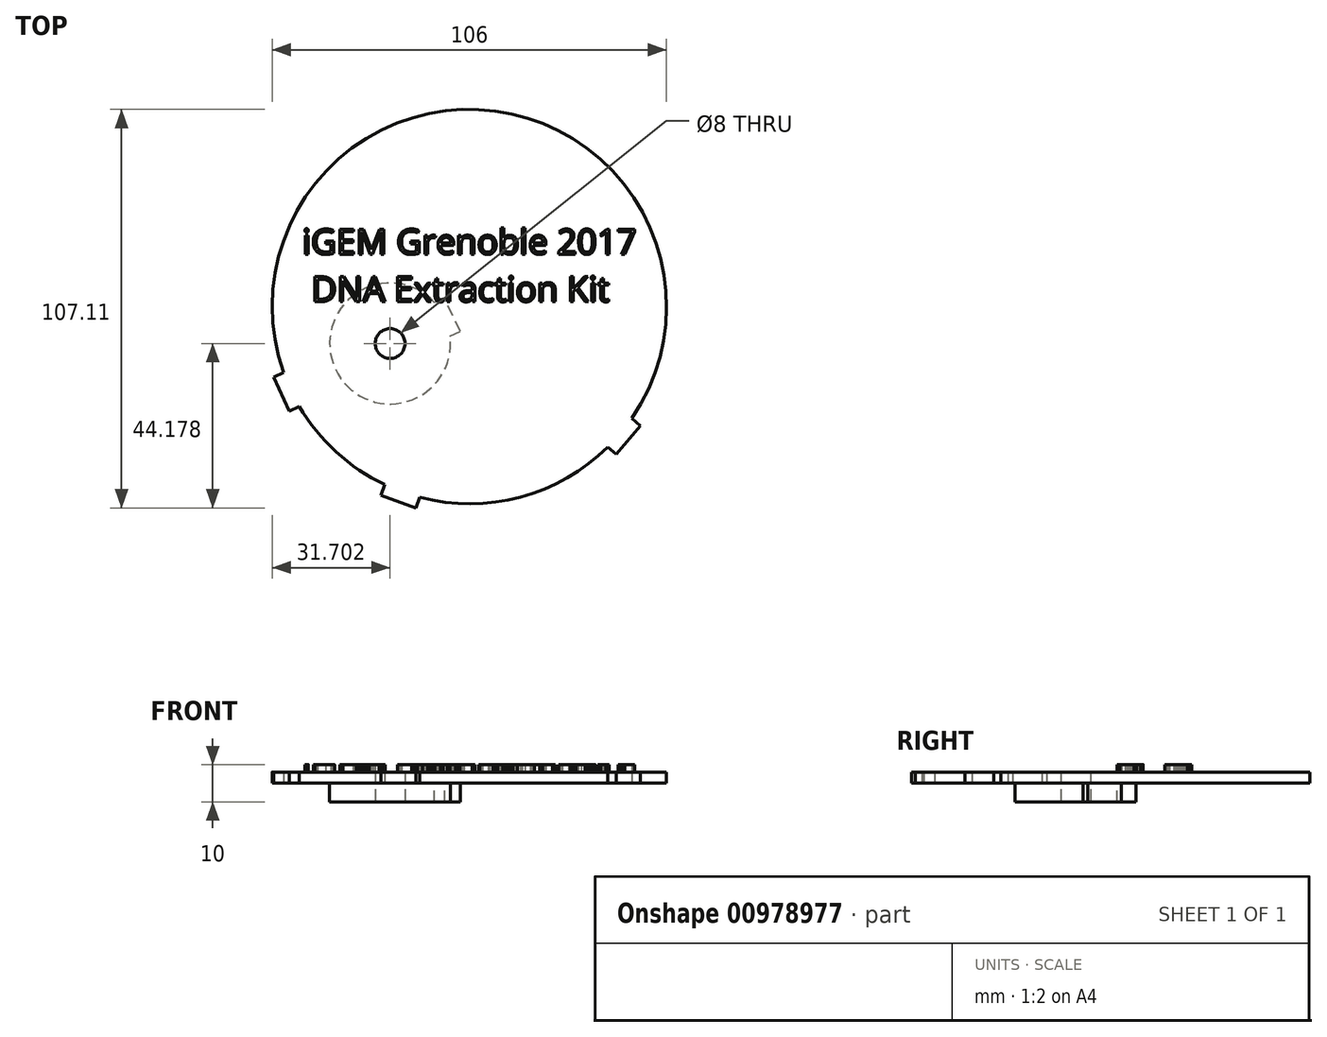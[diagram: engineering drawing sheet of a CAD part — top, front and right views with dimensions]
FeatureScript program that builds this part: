
annotation { "Feature Type Name" : "Feature", "Feature Type Description" : "" }
export const myFeature = defineFeature(function(context is Context, id is Id, definition is map)
    precondition{}
    {
        {
            var Q0;
            Q0=qCreatedBy(makeId("Top.planeOp"),FACE);
            var sketch = newSketch(context, id + "F0", { "sketchPlane" : qUnion([Q0])});
            skCircle(sketch, "E0", {"center": v(0, 0) * mm, "radius": 53 * mm});
            skSolve(sketch);
        }
        {
            var Q0;
            Q0=makeQuery(id+"F0.imprint","IMPRINT",FACE,{"disambiguationData":[TD([[makeQuery(id+"F0.imprint","IMPRINT",EDGE,{"derivedFrom":sQuery(id+"F0.wireOp",EDGE,"E0")}),1.0]])]});
            extrude(context, id + "F1", {"entities" : qUnion([Q0]), "depth" : 3 * mm, "offsetDistance" : 25 * mm});
        }
        {
            var Q0;
            Q0=makeQuery(id+"F1.opExtrude","CAP_FACE",FACE,{"disambiguationData":[OSD([sQuery(id+"F0.wireOp",EDGE,"E0")])],"isStart":true});
            var sketch = newSketch(context, id + "F2", { "sketchPlane" : qUnion([Q0])});
            skCircle(sketch, "E1", {"center": v(-21.3, 9.93) * mm, "radius": 16.25 * mm});
            skLineSegment(sketch, "E2", {"start": v(0, 0) * mm, "end": v(-21.3, 9.93) * mm});
            skLineSegment(sketch, "E3", {"start": v(0, 0) * mm, "end": v(0, 31.72) * mm});
            skLineSegment(sketch, "E4", {"start": v(-5.17, 7.93) * mm, "end": v(-2.45, 6.66) * mm});
            skLineSegment(sketch, "E5", {"start": v(-2.45, 6.66) * mm, "end": v(-6.68, -2.4) * mm});
            skLineSegment(sketch, "E6", {"start": v(-6.68, -2.4) * mm, "end": v(-9.4, -1.13) * mm});
            skLineSegment(sketch, "E7", {"start": v(0, 0) * mm, "end": v(-18.13, 49.8) * mm});
            skLineSegment(sketch, "E8", {"start": v(0, 0) * mm, "end": v(40.6, 34.07) * mm});
            skLineSegment(sketch, "E9", {"start": v(-49.93, 17.77) * mm, "end": v(-52.65, 19.04) * mm});
            skLineSegment(sketch, "E10", {"start": v(-52.65, 19.04) * mm, "end": v(-48.43, 28.1) * mm});
            skLineSegment(sketch, "E11", {"start": v(-48.43, 28.1) * mm, "end": v(-45.7, 26.83) * mm});
            skLineSegment(sketch, "E12", {"start": v(-22.74, 47.87) * mm, "end": v(-23.77, 50.7) * mm});
            skLineSegment(sketch, "E13", {"start": v(-23.77, 50.7) * mm, "end": v(-14.37, 54.11) * mm});
            skLineSegment(sketch, "E14", {"start": v(-14.37, 54.11) * mm, "end": v(-13.35, 51.3) * mm});
            skLineSegment(sketch, "E15", {"start": v(37.2, 37.75) * mm, "end": v(39.5, 39.67) * mm});
            skLineSegment(sketch, "E16", {"start": v(39.5, 39.67) * mm, "end": v(45.93, 32.01) * mm});
            skLineSegment(sketch, "E17", {"start": v(45.93, 32.01) * mm, "end": v(43.63, 30.09) * mm});
            skSolve(sketch);
        }
        {
            var Q0;
            Q0=makeQuery(id+"F2.imprint","IMPRINT",FACE,{"disambiguationData":[TD([[makeQuery(id+"F2.imprint","IMPRINT",EDGE,{"derivedFrom":sQuery(id+"F2.wireOp",EDGE,"E1")}),1.0]])]});
            var Q1;
            {var subQ0=sQuery(id+"F2.wireOp",EDGE,"E6");Q1=makeQuery(id+"F2.imprint","IMPRINT",FACE,{"disambiguationData":[TD([[makeQuery(id+"F2.imprint","IMPRINT",EDGE,{"derivedFrom":subQ0}),-1.0]])]});}
            var Q2;
            {var subQ0=sQuery(id+"F2.wireOp",EDGE,"E4");Q2=makeQuery(id+"F2.imprint","IMPRINT",FACE,{"disambiguationData":[TD([[makeQuery(id+"F2.imprint","IMPRINT",EDGE,{"derivedFrom":subQ0}),-1.0]])]});}
            extrude(context, id + "F3", {"entities" : qUnion([Q0, Q1, Q2]), "operationType" : NewBodyOperationType.ADD, "depth" : 5 * mm, "offsetDistance" : 25 * mm});
        }
        {
            var Q0;
            Q0=makeQuery(id+"F3.opExtrude","CAP_FACE",FACE,{"disambiguationData":[OSD([sQuery(id+"F2.wireOp",EDGE,"E1")])],"isStart":false});
            var sketch = newSketch(context, id + "F4", { "sketchPlane" : qUnion([Q0])});
            skCircle(sketch, "E18", {"center": v(-21.3, 9.93) * mm, "radius": 4 * mm});
            skSolve(sketch);
        }
        {
            var Q0;
            Q0=makeQuery(id+"F4.imprint","IMPRINT",FACE,{"disambiguationData":[TD([[makeQuery(id+"F4.imprint","IMPRINT",EDGE,{"derivedFrom":sQuery(id+"F4.wireOp",EDGE,"E18")}),1.0]])]});
            extrude(context, id + "F5", {"entities" : qUnion([Q0]), "operationType" : NewBodyOperationType.REMOVE, "oppositeDirection" : true, "depth" : 25 * mm, "offsetDistance" : 25 * mm});
        }
        {
            var Q0;
            {var subQ0=sQuery(id+"F2.wireOp",EDGE,"E9");Q0=makeQuery(id+"F2.imprint","IMPRINT",FACE,{"disambiguationData":[TD([[makeQuery(id+"F2.imprint","IMPRINT",EDGE,{"derivedFrom":subQ0}),-1.0]])]});}
            var Q1;
            {var subQ2=sQuery(id+"F2.wireOp",EDGE,"E12");Q1=makeQuery(id+"F2.imprint","IMPRINT",FACE,{"disambiguationData":[TD([[makeQuery(id+"F2.imprint","IMPRINT",EDGE,{"derivedFrom":subQ2}),-1.0]])]});}
            var Q2;
            {var subQ2=sQuery(id+"F2.wireOp",EDGE,"E15");Q2=makeQuery(id+"F2.imprint","IMPRINT",FACE,{"disambiguationData":[TD([[makeQuery(id+"F2.imprint","IMPRINT",EDGE,{"derivedFrom":subQ2}),-1.0]])]});}
            extrude(context, id + "F6", {"entities" : qUnion([Q0, Q1, Q2]), "operationType" : NewBodyOperationType.ADD, "oppositeDirection" : true, "depth" : 3 * mm, "offsetDistance" : 25 * mm});
        }
        {
            var Q0;
            {var subQ0=sQuery(id+"F0.wireOp",EDGE,"E0");Q0=makeQuery(id+"F6.boolean.opBoolean","MERGE",FACE,{"derivedFrom":[makeQuery(id+"F1.opExtrude","CAP_FACE",FACE,{"disambiguationData":[OSD([subQ0])],"isStart":false}),makeQuery(id+"F6.opExtrude","CAP_FACE",FACE,{"disambiguationData":[OSD([subQ0,sQuery(id+"F2.wireOp",EDGE,"E9"),sQuery(id+"F2.wireOp",EDGE,"E10"),sQuery(id+"F2.wireOp",EDGE,"E11")])],"isStart":false}),makeQuery(id+"F6.opExtrude","CAP_FACE",FACE,{"disambiguationData":[OSD([subQ0,sQuery(id+"F2.wireOp",EDGE,"E12"),sQuery(id+"F2.wireOp",EDGE,"E13"),sQuery(id+"F2.wireOp",EDGE,"E14")])],"isStart":false}),makeQuery(id+"F6.opExtrude","CAP_FACE",FACE,{"disambiguationData":[OSD([subQ0,sQuery(id+"F2.wireOp",EDGE,"E15"),sQuery(id+"F2.wireOp",EDGE,"E16"),sQuery(id+"F2.wireOp",EDGE,"E17")])],"isStart":false})]});}
            var sketch = newSketch(context, id + "F7", { "sketchPlane" : qUnion([Q0])});
            skText(sketch, "E19", { "text": "iGEM Grenoble 2017\n DNA Extraction Kit", "fontName": "OpenSans-Regular.ttf"});
            const initialGuessF7  = {"E19": [-0.04492, 0.01408, 1, 0, 0.00675]};
            skSetInitialGuess(sketch, initialGuessF7);
            skSolve(sketch);
        }
        {
            var Q0;
            Q0=makeQuery(id+"F7.imprint","IMPRINT",FACE,{"disambiguationData":[TD([[makeQuery(id+"F7.imprint","IMPRINT",EDGE,{"derivedFrom":sQuery(id+"F7.wireOp",EDGE,"E19.sketch_text.stroke-0")}),-1.0]])]});
            var Q1;
            Q1=makeQuery(id+"F7.imprint","IMPRINT",FACE,{"disambiguationData":[TD([[makeQuery(id+"F7.imprint","IMPRINT",EDGE,{"derivedFrom":sQuery(id+"F7.wireOp",EDGE,"E19.sketch_text.stroke-4")}),-1.0]])]});
            var Q2;
            Q2=makeQuery(id+"F7.imprint","IMPRINT",FACE,{"disambiguationData":[TD([[makeQuery(id+"F7.imprint","IMPRINT",EDGE,{"derivedFrom":sQuery(id+"F7.wireOp",EDGE,"E19.sketch_text.stroke-12")}),-1.0]])]});
            var Q3;
            Q3=makeQuery(id+"F7.imprint","IMPRINT",FACE,{"disambiguationData":[TD([[makeQuery(id+"F7.imprint","IMPRINT",EDGE,{"derivedFrom":sQuery(id+"F7.wireOp",EDGE,"E19.sketch_text.stroke-32")}),-1.0]])]});
            var Q4;
            Q4=makeQuery(id+"F7.imprint","IMPRINT",FACE,{"disambiguationData":[TD([[makeQuery(id+"F7.imprint","IMPRINT",EDGE,{"derivedFrom":sQuery(id+"F7.wireOp",EDGE,"E19.sketch_text.stroke-44")}),-1.0]])]});
            var Q5;
            Q5=makeQuery(id+"F7.imprint","IMPRINT",FACE,{"disambiguationData":[TD([[makeQuery(id+"F7.imprint","IMPRINT",EDGE,{"derivedFrom":sQuery(id+"F7.wireOp",EDGE,"E19.sketch_text.stroke-62")}),-1.0]])]});
            var Q6;
            Q6=makeQuery(id+"F7.imprint","IMPRINT",FACE,{"disambiguationData":[TD([[makeQuery(id+"F7.imprint","IMPRINT",EDGE,{"derivedFrom":sQuery(id+"F7.wireOp",EDGE,"E19.sketch_text.stroke-82")}),-1.0]])]});
            var Q7;
            Q7=makeQuery(id+"F7.imprint","IMPRINT",FACE,{"disambiguationData":[TD([[makeQuery(id+"F7.imprint","IMPRINT",EDGE,{"derivedFrom":sQuery(id+"F7.wireOp",EDGE,"E19.sketch_text.stroke-95")}),-1.0]])]});
            var Q8;
            Q8=makeQuery(id+"F7.imprint","IMPRINT",FACE,{"disambiguationData":[TD([[makeQuery(id+"F7.imprint","IMPRINT",EDGE,{"derivedFrom":sQuery(id+"F7.wireOp",EDGE,"E19.sketch_text.stroke-114")}),-1.0]])]});
            var Q9;
            Q9=makeQuery(id+"F7.imprint","IMPRINT",FACE,{"disambiguationData":[TD([[makeQuery(id+"F7.imprint","IMPRINT",EDGE,{"derivedFrom":sQuery(id+"F7.wireOp",EDGE,"E19.sketch_text.stroke-131")}),-1.0]])]});
            var Q10;
            Q10=makeQuery(id+"F7.imprint","IMPRINT",FACE,{"disambiguationData":[TD([[makeQuery(id+"F7.imprint","IMPRINT",EDGE,{"derivedFrom":sQuery(id+"F7.wireOp",EDGE,"E19.sketch_text.stroke-148")}),-1.0]])]});
            var Q11;
            Q11=makeQuery(id+"F7.imprint","IMPRINT",FACE,{"disambiguationData":[TD([[makeQuery(id+"F7.imprint","IMPRINT",EDGE,{"derivedFrom":sQuery(id+"F7.wireOp",EDGE,"E19.sketch_text.stroke-171")}),-1.0]])]});
            var Q12;
            Q12=makeQuery(id+"F7.imprint","IMPRINT",FACE,{"disambiguationData":[TD([[makeQuery(id+"F7.imprint","IMPRINT",EDGE,{"derivedFrom":sQuery(id+"F7.wireOp",EDGE,"E19.sketch_text.stroke-175")}),-1.0]])]});
            var Q13;
            Q13=makeQuery(id+"F7.imprint","IMPRINT",FACE,{"disambiguationData":[TD([[makeQuery(id+"F7.imprint","IMPRINT",EDGE,{"derivedFrom":sQuery(id+"F7.wireOp",EDGE,"E19.sketch_text.stroke-194")}),-1.0]])]});
            var Q14;
            Q14=makeQuery(id+"F7.imprint","IMPRINT",FACE,{"disambiguationData":[TD([[makeQuery(id+"F7.imprint","IMPRINT",EDGE,{"derivedFrom":sQuery(id+"F7.wireOp",EDGE,"E19.sketch_text.stroke-214")}),-1.0]])]});
            var Q15;
            Q15=makeQuery(id+"F7.imprint","IMPRINT",FACE,{"disambiguationData":[TD([[makeQuery(id+"F7.imprint","IMPRINT",EDGE,{"derivedFrom":sQuery(id+"F7.wireOp",EDGE,"E19.sketch_text.stroke-230")}),-1.0]])]});
            var Q16;
            Q16=makeQuery(id+"F7.imprint","IMPRINT",FACE,{"disambiguationData":[TD([[makeQuery(id+"F7.imprint","IMPRINT",EDGE,{"derivedFrom":sQuery(id+"F7.wireOp",EDGE,"E19.sketch_text.stroke-239")}),-1.0]])]});
            var Q17;
            Q17=makeQuery(id+"F7.imprint","IMPRINT",FACE,{"disambiguationData":[TD([[makeQuery(id+"F7.imprint","IMPRINT",EDGE,{"derivedFrom":sQuery(id+"F7.wireOp",EDGE,"E19.sketch_text.stroke-246")}),-1.0]])]});
            var Q18;
            Q18=makeQuery(id+"F7.imprint","IMPRINT",FACE,{"disambiguationData":[TD([[makeQuery(id+"F7.imprint","IMPRINT",EDGE,{"derivedFrom":sQuery(id+"F7.wireOp",EDGE,"E19.sketch_text.stroke-260")}),-1.0]])]});
            var Q19;
            Q19=makeQuery(id+"F7.imprint","IMPRINT",FACE,{"disambiguationData":[TD([[makeQuery(id+"F7.imprint","IMPRINT",EDGE,{"derivedFrom":sQuery(id+"F7.wireOp",EDGE,"E19.sketch_text.stroke-275")}),-1.0]])]});
            var Q20;
            Q20=makeQuery(id+"F7.imprint","IMPRINT",FACE,{"disambiguationData":[TD([[makeQuery(id+"F7.imprint","IMPRINT",EDGE,{"derivedFrom":sQuery(id+"F7.wireOp",EDGE,"E19.sketch_text.stroke-288")}),-1.0]])]});
            var Q21;
            Q21=makeQuery(id+"F7.imprint","IMPRINT",FACE,{"disambiguationData":[TD([[makeQuery(id+"F7.imprint","IMPRINT",EDGE,{"derivedFrom":sQuery(id+"F7.wireOp",EDGE,"E19.sketch_text.stroke-300")}),-1.0]])]});
            var Q22;
            Q22=makeQuery(id+"F7.imprint","IMPRINT",FACE,{"disambiguationData":[TD([[makeQuery(id+"F7.imprint","IMPRINT",EDGE,{"derivedFrom":sQuery(id+"F7.wireOp",EDGE,"E19.sketch_text.stroke-312")}),-1.0]])]});
            var Q23;
            Q23=makeQuery(id+"F7.imprint","IMPRINT",FACE,{"disambiguationData":[TD([[makeQuery(id+"F7.imprint","IMPRINT",EDGE,{"derivedFrom":sQuery(id+"F7.wireOp",EDGE,"E19.sketch_text.stroke-327")}),-1.0]])]});
            var Q24;
            Q24=makeQuery(id+"F7.imprint","IMPRINT",FACE,{"disambiguationData":[TD([[makeQuery(id+"F7.imprint","IMPRINT",EDGE,{"derivedFrom":sQuery(id+"F7.wireOp",EDGE,"E19.sketch_text.stroke-346")}),-1.0]])]});
            var Q25;
            Q25=makeQuery(id+"F7.imprint","IMPRINT",FACE,{"disambiguationData":[TD([[makeQuery(id+"F7.imprint","IMPRINT",EDGE,{"derivedFrom":sQuery(id+"F7.wireOp",EDGE,"E19.sketch_text.stroke-359")}),-1.0]])]});
            var Q26;
            Q26=makeQuery(id+"F7.imprint","IMPRINT",FACE,{"disambiguationData":[TD([[makeQuery(id+"F7.imprint","IMPRINT",EDGE,{"derivedFrom":sQuery(id+"F7.wireOp",EDGE,"E19.sketch_text.stroke-386")}),-1.0]])]});
            var Q27;
            Q27=makeQuery(id+"F7.imprint","IMPRINT",FACE,{"disambiguationData":[TD([[makeQuery(id+"F7.imprint","IMPRINT",EDGE,{"derivedFrom":sQuery(id+"F7.wireOp",EDGE,"E19.sketch_text.stroke-401")}),-1.0]])]});
            var Q28;
            Q28=makeQuery(id+"F7.imprint","IMPRINT",FACE,{"disambiguationData":[TD([[makeQuery(id+"F7.imprint","IMPRINT",EDGE,{"derivedFrom":sQuery(id+"F7.wireOp",EDGE,"E19.sketch_text.stroke-420")}),-1.0]])]});
            var Q29;
            Q29=makeQuery(id+"F7.imprint","IMPRINT",FACE,{"disambiguationData":[TD([[makeQuery(id+"F7.imprint","IMPRINT",EDGE,{"derivedFrom":sQuery(id+"F7.wireOp",EDGE,"E19.sketch_text.stroke-424")}),-1.0]])]});
            var Q30;
            Q30=makeQuery(id+"F7.imprint","IMPRINT",FACE,{"disambiguationData":[TD([[makeQuery(id+"F7.imprint","IMPRINT",EDGE,{"derivedFrom":sQuery(id+"F7.wireOp",EDGE,"E19.sketch_text.stroke-432")}),-1.0]])]});
            var Q31;
            Q31=makeQuery(id+"F7.imprint","IMPRINT",FACE,{"disambiguationData":[TD([[makeQuery(id+"F7.imprint","IMPRINT",EDGE,{"derivedFrom":sQuery(id+"F7.wireOp",EDGE,"E19.sketch_text.stroke-449")}),-1.0]])]});
            var Q32;
            Q32=makeQuery(id+"F7.imprint","IMPRINT",FACE,{"disambiguationData":[TD([[makeQuery(id+"F7.imprint","IMPRINT",EDGE,{"derivedFrom":sQuery(id+"F7.wireOp",EDGE,"E19.sketch_text.stroke-466")}),-1.0]])]});
            var Q33;
            Q33=makeQuery(id+"F7.imprint","IMPRINT",FACE,{"disambiguationData":[TD([[makeQuery(id+"F7.imprint","IMPRINT",EDGE,{"derivedFrom":sQuery(id+"F7.wireOp",EDGE,"E19.sketch_text.stroke-478")}),-1.0]])]});
            var Q34;
            Q34=makeQuery(id+"F7.imprint","IMPRINT",FACE,{"disambiguationData":[TD([[makeQuery(id+"F7.imprint","IMPRINT",EDGE,{"derivedFrom":sQuery(id+"F7.wireOp",EDGE,"E19.sketch_text.stroke-482")}),-1.0]])]});
            var Q35;
            Q35=makeQuery(id+"F7.imprint","IMPRINT",FACE,{"disambiguationData":[TD([[makeQuery(id+"F7.imprint","IMPRINT",EDGE,{"derivedFrom":sQuery(id+"F7.wireOp",EDGE,"E19.sketch_text.stroke-490")}),-1.0]])]});
            var Q36;
            Q36=makeQuery(id+"F7.imprint","IMPRINT",FACE,{"disambiguationData":[TD([[makeQuery(id+"F7.imprint","IMPRINT",EDGE,{"derivedFrom":sQuery(id+"F7.wireOp",EDGE,"E19.sketch_text.stroke-331")}),-1.0]])]});
            var Q37;
            Q37=makeQuery(id+"F7.imprint","IMPRINT",FACE,{"disambiguationData":[TD([[makeQuery(id+"F7.imprint","IMPRINT",EDGE,{"derivedFrom":sQuery(id+"F7.wireOp",EDGE,"E19.sketch_text.stroke-371")}),-1.0]])]});
            var Q38;
            Q38=makeQuery(id+"F7.imprint","IMPRINT",FACE,{"disambiguationData":[TD([[makeQuery(id+"F7.imprint","IMPRINT",EDGE,{"derivedFrom":sQuery(id+"F7.wireOp",EDGE,"E19.sketch_text.stroke-405")}),-1.0]])]});
            var Q39;
            Q39=makeQuery(id+"F7.imprint","IMPRINT",FACE,{"disambiguationData":[TD([[makeQuery(id+"F7.imprint","IMPRINT",EDGE,{"derivedFrom":sQuery(id+"F7.wireOp",EDGE,"E19.sketch_text.stroke-409")}),-1.0]])]});
            var Q40;
            Q40=makeQuery(id+"F7.imprint","IMPRINT",FACE,{"disambiguationData":[TD([[makeQuery(id+"F7.imprint","IMPRINT",EDGE,{"derivedFrom":sQuery(id+"F7.wireOp",EDGE,"E19.sketch_text.stroke-467")}),-1.0]])]});
            var Q41;
            Q41=makeQuery(id+"F7.imprint","IMPRINT",FACE,{"disambiguationData":[TD([[makeQuery(id+"F7.imprint","IMPRINT",EDGE,{"derivedFrom":sQuery(id+"F7.wireOp",EDGE,"E19.sketch_text.stroke-451")}),-1.0]])]});
            extrude(context, id + "F8", {"entities" : qUnion([Q0, Q1, Q2, Q3, Q4, Q5, Q6, Q7, Q8, Q9, Q10, Q11, Q12, Q13, Q14, Q15, Q16, Q17, Q18, Q19, Q20, Q21, Q22, Q23, Q24, Q25, Q26, Q27, Q28, Q29, Q30, Q31, Q32, Q33, Q34, Q35, Q36, Q37, Q38, Q39, Q40, Q41]), "operationType" : NewBodyOperationType.ADD, "depth" : 2 * mm, "offsetDistance" : 25 * mm});
        }
    });
